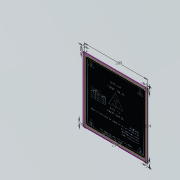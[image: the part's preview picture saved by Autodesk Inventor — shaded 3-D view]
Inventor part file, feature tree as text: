
AUTODESK INVENTOR PART (.ipt)
format: ipt  version: 2016 (Build 200138000, 138)  size: 300,032 bytes
history: native  units: mm
features: sketch x1, extrude x1, hole x1, other x1
ambient origin geometry x8: Origin, YZ Plane, XZ Plane, XY Plane, X Axis, Y Axis, Z Axis, Center Point
bodies: Solid1 (feature_tree)
feature tree (4):
  sketch  "Sketch1"  dims[d0=214.0mm d1=214.0mm d2=209.0mm d3=5.0mm d4=5.0mm d5=5.0mm d6=5.0mm d7=5.0mm d8=5.0mm d9=5.0mm d10=3.0mm d11=0.0mm d12=3.2mm d13=6.0mm d14=4.0mm d15=2.0mm d16=90.0deg d17=8.0mm d18=20.594885mm]
  extrude  "Extrusion1"  Depth=214.0mm
  hole  "Hole1"  [1 undecoded]
  other  "Image3"
note: 1 required parameter value undecoded (feature->parameter linkage not recoverable at this tier; creation-order binding heuristic only, values carry confidence <= 0.55)
